# Revit family: НЕВАТОМ_Фильтр-бокс AxB FVGU, Версия 2
name_source: partatom
category: Арматура воздуховодов
revit_build: Autodesk Revit 2017 (Build: 20170118_1100(x64)
units: mm (PartAtom-declared; Revit-internal decimal feet)

## family parameters
Всегда вертикально = Нет
На основе рабочей плоскости = Нет
Общий = Нет
При загрузке вырезать с полостями = Нет
Размер круглого соединителя = Использовать диаметр
Тип детали = Вставляется

## types (14) — shared parameters
ADSK_Единица измерения = шт.
ADSK_Завод-изготовитель = НЕВАТОМ
ADSK_Количество = 1
ADSK_Материал наименование = Оцинкованная сталь
L = 200 мм
Nevatom_URL = https://t.me
t = 2 мм
Материал корпуса = Оцинкованная сталь
НЕВАТОМ_Сменная кассета = FVGU
zero-valued in all types: ADSK_Масса

## per-type parameters (varying)
| type | ADSK_Марка | ADSK_Расход воздуха |
| ФИЛЬТР-БОКС FVGU–200х200 | FVGU–200х200 | 350.0 м³/ч |
| ФИЛЬТР-БОКС FVGU–250х250 | FVGU–250х250 | 550.0 м³/ч |
| ФИЛЬТР-БОКС FVGU-300х150 | FVGU-300х150 | 400.0 м³/ч |
| ФИЛЬТР-БОКС FVGU–300х200 | FVGU–300х200 | 550.0 м³/ч |
| ФИЛЬТР-БОКС FVGU–300х300 | FVGU–300х300 | 800.0 м³/ч |
| ФИЛЬТР-БОКС FVGU–400х200 | FVGU–400х200 | 720.0 м³/ч |
| ФИЛЬТР-БОКС FVGU–500х250 | FVGU–500х250 | 1100.0 м³/ч |
| ФИЛЬТР-БОКС FVGU–500х300 | FVGU–500х300 | 1300.0 м³/ч |
| ФИЛЬТР-БОКС FVGU–600х300 | FVGU–600х300 | 1600.0 м³/ч |
| ФИЛЬТР-БОКС FVGU–600x350 | FVGU–600x350 | 1800.0 м³/ч |
| ФИЛЬТР-БОКС FVGU–700x400 | FVGU–700x400 | 2500.0 м³/ч |
| ФИЛЬТР-БОКС FVGU–800x500 | FVGU–800x500 | 3600.0 м³/ч |
| ФИЛЬТР-БОКС FVGU–900x500 | FVGU–900x500 | 4000.0 м³/ч |
| ФИЛЬТР-БОКС FVGU–1000x500 | FVGU–1000x500 | 4500.0 м³/ч |
